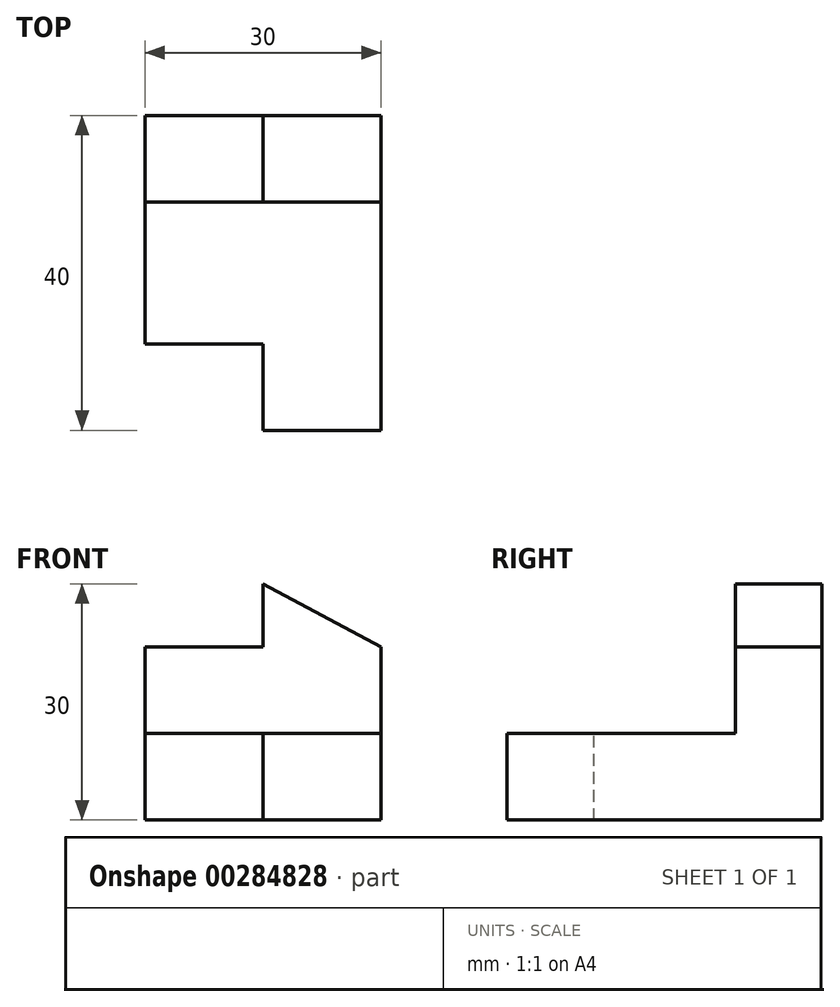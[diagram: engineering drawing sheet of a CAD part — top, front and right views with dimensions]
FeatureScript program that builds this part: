
annotation { "Feature Type Name" : "Feature", "Feature Type Description" : "" }
export const myFeature = defineFeature(function(context is Context, id is Id, definition is map)
    precondition{}
    {
        {
            var Q0;
            Q0=qCreatedBy(makeId("Front.planeOp"),FACE);
            var sketch = newSketch(context, id + "F0", { "sketchPlane" : qUnion([Q0])});
            skLineSegment(sketch, "E0.bottom", {"start": v(0, 0) * mm, "end": v(40, 0) * mm});
            skLineSegment(sketch, "E0.top", {"start": v(0, 30) * mm, "end": v(40, 30) * mm});
            skLineSegment(sketch, "E0.left", {"start": v(0, 0) * mm, "end": v(0, 30) * mm});
            skLineSegment(sketch, "E0.right", {"start": v(40, 0) * mm, "end": v(40, 30) * mm});
            skLineSegment(sketch, "E1.bottom", {"start": v(40, 30) * mm, "end": v(11, 30) * mm});
            skLineSegment(sketch, "E1.top", {"start": v(40, 11) * mm, "end": v(11, 11) * mm});
            skLineSegment(sketch, "E1.left", {"start": v(40, 30) * mm, "end": v(40, 11) * mm});
            skLineSegment(sketch, "E1.right", {"start": v(11, 30) * mm, "end": v(11, 11) * mm});
            skSolve(sketch);
        }
        {
            var Q0;
            Q0=makeQuery(id+"F0.imprint","IMPRINT",FACE,{"disambiguationData":[TD([[makeQuery(id+"F0.imprint","IMPRINT",EDGE,{"derivedFrom":sQuery(id+"F0.wireOp",EDGE,"E0.bottom")}),1.0]])]});
            extrude(context, id + "F1", {"entities" : qUnion([Q0]), "depth" : 30 * mm});
        }
        {
            var Q0;
            Q0=makeQuery(id+"F1.opExtrude","SWEPT_FACE",FACE,{"disambiguationData":[OSD([sQuery(id+"F0.wireOp",EDGE,"E1.top")])]});
            var sketch = newSketch(context, id + "F2", { "sketchPlane" : qUnion([Q0])});
            skPoint(sketch, "E2.oppositeSnap0", {"position": v(40, -15) * mm});
            skLineSegment(sketch, "E2.bottom", {"start": v(40, -30) * mm, "end": v(29, -30) * mm});
            skLineSegment(sketch, "E2.top", {"start": v(40, -15) * mm, "end": v(29, -15) * mm});
            skLineSegment(sketch, "E2.left", {"start": v(40, -30) * mm, "end": v(40, -15) * mm});
            skLineSegment(sketch, "E2.right", {"start": v(29, -30) * mm, "end": v(29, -15) * mm});
            skSolve(sketch);
        }
        {
            var Q0;
            Q0=qSketchRegion(id+"F2",true);
            var Q1;
            Q1=makeQuery(id+"F1.opExtrude","CAP_VERTEX",VERTEX,{"disambiguationData":[OSD([sQuery(id+"F0.wireOp",EDGE,"E0.bottom"),sQuery(id+"F0.wireOp",EDGE,"E0.right")])],"isStart":false});
            extrude(context, id + "F3", {"entities" : qUnion([Q0]), "operationType" : NewBodyOperationType.REMOVE, "endBound" : BoundingType.UP_TO_VERTEX, "oppositeDirection" : true, "endBoundEntityVertex" : qUnion([Q1]), "depth" : 25 * mm});
        }
        {
            var Q0;
            Q0=makeQuery(id+"F1.opExtrude","SWEPT_FACE",FACE,{"disambiguationData":[OSD([sQuery(id+"F0.wireOp",EDGE,"E1.right")])]});
            var sketch = newSketch(context, id + "F4", { "sketchPlane" : qUnion([Q0])});
            skPoint(sketch, "E3.oppositeSnap0", {"position": v(-15, 30) * mm});
            skLineSegment(sketch, "E3.bottom", {"start": v(-30, 30) * mm, "end": v(-15, 30) * mm});
            skLineSegment(sketch, "E3.top", {"start": v(-30, 22) * mm, "end": v(-15, 22) * mm});
            skLineSegment(sketch, "E3.left", {"start": v(-30, 30) * mm, "end": v(-30, 22) * mm});
            skLineSegment(sketch, "E3.right", {"start": v(-15, 30) * mm, "end": v(-15, 22) * mm});
            skSolve(sketch);
        }
        {
            var Q0;
            Q0=qSketchRegion(id+"F4",true);
            var Q1;
            Q1=makeQuery(id+"F1.opExtrude","CAP_VERTEX",VERTEX,{"disambiguationData":[OSD([sQuery(id+"F0.wireOp",EDGE,"E0.top"),sQuery(id+"F0.wireOp",EDGE,"E0.left")])],"isStart":false});
            extrude(context, id + "F5", {"entities" : qUnion([Q0]), "operationType" : NewBodyOperationType.REMOVE, "endBound" : BoundingType.UP_TO_VERTEX, "oppositeDirection" : true, "endBoundEntityVertex" : qUnion([Q1]), "depth" : 25 * mm});
        }
        {
            var Q0;
            Q0=makeQuery(id+"F1.opExtrude","SWEPT_BODY",BODY,{"disambiguationData":[OSD([sQuery(id+"F0.wireOp",EDGE,"E0.bottom"),sQuery(id+"F0.wireOp",EDGE,"E0.top"),sQuery(id+"F0.wireOp",EDGE,"E0.left"),sQuery(id+"F0.wireOp",EDGE,"E0.right"),sQuery(id+"F0.wireOp",EDGE,"E1.top"),sQuery(id+"F0.wireOp",EDGE,"E1.right")])]});
            var Q1;
            Q1=makeQuery(id+"F1.opExtrude","CAP_EDGE",EDGE,{"disambiguationData":[OSD([sQuery(id+"F0.wireOp",EDGE,"E0.left")])],"isStart":true});
            transform(context, id + "F6", {"entities" : qUnion([Q0]), "transformType" : TransformType.ROTATION, "transformAxis" : qUnion([Q1]), "angle" : 90 * degree, "oppositeDirection" : true, "makeCopy" : false});
        }
        {
            var Q0;
            Q0=makeQuery(id+"F1.opExtrude","SWEPT_FACE",FACE,{"disambiguationData":[OSD([sQuery(id+"F0.wireOp",EDGE,"E1.right")])]});
            var sketch = newSketch(context, id + "F7", { "sketchPlane" : qUnion([Q0])});
            skLineSegment(sketch, "E4", {"start": v(-15, 30) * mm, "end": v(0, 22) * mm});
            skLineSegment(sketch, "E5", {"start": v(-15, 22) * mm, "end": v(0, 30) * mm});
            skSolve(sketch);
        }
        {
            var Q0;
            {var subQ1=sQuery(id+"F0.wireOp",EDGE,"E1.right");var subQ2=makeQuery(id+"F1.opExtrude","SWEPT_EDGE",EDGE,{"disambiguationData":[OSD([sQuery(id+"F0.wireOp",EDGE,"E0.top"),sQuery(id+"F0.wireOp",EDGE,"E1.bottom"),subQ1])]});Q0=makeQuery(id+"F7.imprint","IMPRINT",FACE,{"disambiguationData":[TD([[makeQuery(id+"F7.imprint","IMPRINT",EDGE,{"derivedFrom":subQ2}),-1.0]])]});}
            var Q1;
            {var subQ0=sQuery(id+"F7.wireOp",EDGE,"E4");var subQ1=sQuery(id+"F0.wireOp",EDGE,"E1.right");var subQ2=makeQuery(id+"F1.opExtrude","CAP_EDGE",EDGE,{"disambiguationData":[OSD([subQ1])],"isStart":true});var subQ3=makeQuery(id+"F7.imprint","INTERSECT",VERTEX,{"derivedFrom":[subQ2,subQ0]});Q1=makeQuery(id+"F7.imprint","IMPRINT",FACE,{"disambiguationData":[TD([[makeQuery(id+"F7.imprint","IMPRINT",EDGE,{"disambiguationData":[TD([[subQ3,1.0]])],"derivedFrom":subQ0}),1.0]])]});}
            extrude(context, id + "F8", {"entities" : qUnion([Q0, Q1]), "operationType" : NewBodyOperationType.REMOVE, "endBound" : BoundingType.THROUGH_ALL, "oppositeDirection" : true, "depth" : 25 * mm});
        }
    });
